# Revit family: CCE
name_source: partatom
category: Lighting Fixtures
units: mm (PartAtom-declared; Revit-internal decimal feet)

## family parameters
Cut with Voids When Loaded = No
Host = Face
Light Source = Yes
OmniClass Number = 23.80.70.11.21
OmniClass Title = Emergency Lighting
Part Type = Normal
Room Calculation Point = No
Round Connector Dimension = Use Diameter
Shared = No

## types (8) — shared parameters
120 Voltage = Yes
277 Voltage = No
Apparent Load = 1 VA
Assembly Code = D5020200
Color Filter = 16777215
Default Elevation = 48.000"
Dimming Lamp Color Temperature Shift = <None>
Emit Shape Visible in Rendering = No
Finish = White
Housing Material = Black
Lamp = LED Lamp
Load Classification = Lighting
Manufacturer = Compass Products
Photometric Web File = generic
URL = https://www.currentlighting.com
Voltage = 120 V
Wattage Comments = 1 W

## per-type parameters (varying)
| type | Description | Double Face | Emit from Rectangle Length | Emit from Rectangle Width | Lens | Single Face | Tilt Angle | zz Length 1 |
| CCESRE | Brushed Face, Black Housing, Single-Face, Red, Emergency | No | 48.000" | 24.000" | Red LED | Yes | 60.00° | 0.250" |
| CCEDRE | Brushed Face, Black Housing, Double-Face, Red, Emergency | Yes | 11.000" | 7.750" | Red LED | No | 60.00° | 0.438" |
| CCESGE | Brushed Face, Black Housing, Single-Face, Green, Emergency | No | 48.000" | 24.000" | Green LED | Yes | 60.00° | 0.250" |
| CCEDGE | Brushed Face, Black Housing, Double-Face, Green, Emergency | Yes | 48.000" | 24.000" | Green LED | No | 60.00° | 0.438" |
| CCESR | Brushed Face, Black Housing, Single-Face, Red, AC | No | 10.000" | 7.000" | Red LED | Yes | 0.00° | 0.250" |
| CCEDR | Brushed Face, Black Housing, Double-Face, Red, AC | Yes | 48.000" | 24.000" | Red LED | No | 60.00° | 0.438" |
| CCESG | Brushed Face, Black Housing, Single-Face, Green, AC | No | 48.000" | 24.000" | Green LED | Yes | 60.00° | 0.250" |
| CCEDG | Brushed Face, Black Housing, Double-Face, Green, AC | Yes | 5.000" | 5.000" | Green LED | No | 90.00° | 0.438" |

note: column(s) folded — value = type name in every type: Model

## geometry (parser evidence)
native form markers: Sweep x3
no freeform markers — native parametric forms only
